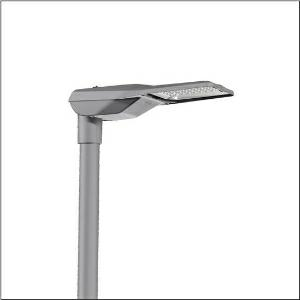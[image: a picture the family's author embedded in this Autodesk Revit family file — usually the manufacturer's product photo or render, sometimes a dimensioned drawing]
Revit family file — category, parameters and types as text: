
# Revit family: streetlight_sl_21_mini___stw1_0a_5xe2e33s08jb_3b81
name_source: partatom
category: Lighting Fixtures
units: mm (PartAtom-declared; Revit-internal decimal feet)

## family parameters
Cut with Voids When Loaded = No
Host = Face
Light Source = No
Part Type = Normal
Room Calculation Point = No
Round Connector Dimension = Use Diameter
Shared = No

## types (1)
- --- (1 x LED, 12940 lm, 88.6 W, 3000K)
    Apparent Load = 89 VA
    CIE Flux Codes = 39 75 98 100 100
    Color Rendering = 70
    Color Temperature = 3000K
    Default Elevation = 1800 mm
    Description = Streetlight SL 21 mini, mast luminaire, primary light control with lens, of PMMA, primary optical cover: cover, of toughened safety glass, transparent, light distribution: STW1.0a, light emission: direct distribution, primary light characteristic: asymmetric, installation type: side-entry, post-top, LED, High Power LED, rated luminous flux: 12.940lm, luminous efficacy: 146lm/W, light colour: 730, colour temperature: 3000K, control gear: D4i, control: overheat protection, constant luminous flux control, time-dependent luminous flux control, flexible luminous flux parameterisation, pre-setting: logarithmic dimming characteristic, mains connection: 220..240V, AC, 50/60Hz, start of lifetime: 89W, end of service life: 92W, reduction: 41W, luminaire housing, of diecast aluminium, powder-coated, Siteco® metallic grey (DB 702S), corrosivity category C5 mid according to DIN EN ISO 12944, please order mast flange separately, inclination adjustable: 0°, 5°, 10°, 15°, sealing non-destructively replaceable, multi-level sealing system, length: 628mm, width: 235mm, height: 110mm, mast flange for spigot size: 42mm (side-entry): 5XC10008XM4, 60/48mm (side-entry/post-top): 5XC10108XM2, 76/60mm (side-entry/post-top): 5XC10108XM1, mounting height: 4..8m, Smart Interface above, protection rating (complete): IP66, insulation class (complete): insulation class II (safety insulation), certification: CE, ENEC, ENEC+, VDE, impact resistance: IK10, permissible operating ambient temperature for outdoor applications: -40..+50°C, standard-compliant lighting for roads and squares, packaging unit: 1 piece

Light Distribution: STW1.0a
    Height = 110 mm
    Lamp = 1 x LED
    Lamp Light Flux = 12940 lm
    Lamp Power = 88.6 W
    Lamp count = 1
    Length = 625 mm
    Luminous efficacy = 146 lm/W
    Manufacturer = Siteco
    ModVariant = No
    Model = 5XE2E33S08JB
    Number of Poles = 1
    OnlyDefault = Yes
    Power Factor = 1
    Product Name = Streetlight SL 21 mini | STW1.0a
    Product group = mast luminaire | pylon top
    ProductGroupID = 6100
    Protection Class = Protection class II
    Protection Degree = IP 66
    RLX_Detail_Level = 1
    RLX_Emergency_Light_Flux = 0 lm
    RLX_Emergency_Type = 0
    RLX_Emergency_Type_DB = No
    RlxData = <blob elided: 26309 chars, md5=99d6f401>
    Socket = socket
    Standby Power = 0 W
    System Light Flux = 12940 lm
    System Power = 89 W
    Type Comments = factory setting: luminous flux: 100 % | dim-lin: 254 | 915 mA
    Type Image = l_1003515.jpg
    URL = http://relux.com
    VarID = @adj_031363
    Voltage = 0 V
    Weight = 0.00 kg
    Width = 234 mm

## geometry (parser evidence)
native form markers: Blend x4, Sweep x13
no freeform markers — native parametric forms only
